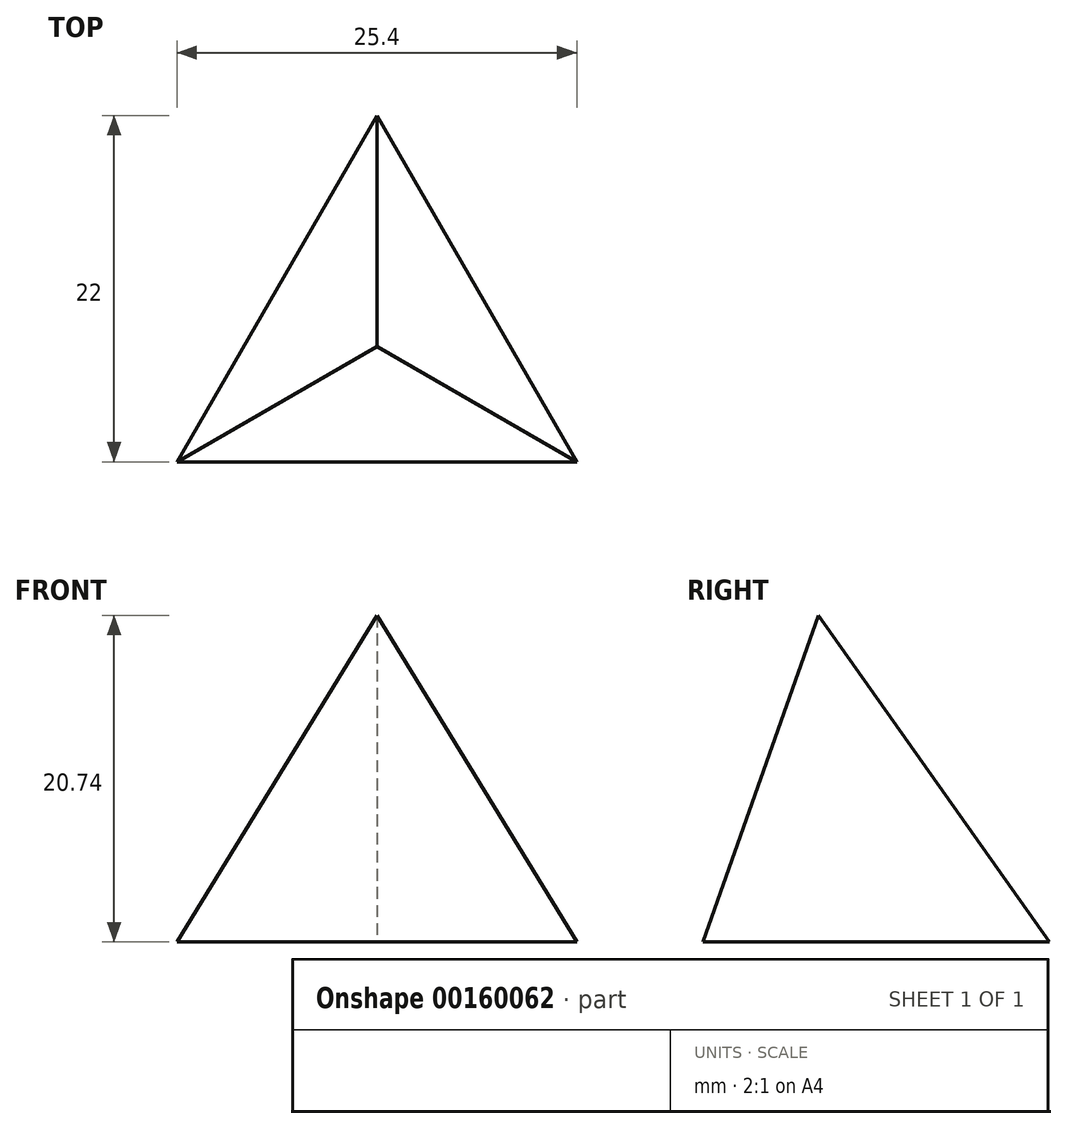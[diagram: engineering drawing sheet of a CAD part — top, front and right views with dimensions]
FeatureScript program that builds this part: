
annotation { "Feature Type Name" : "Feature", "Feature Type Description" : "" }
export const myFeature = defineFeature(function(context is Context, id is Id, definition is map)
    precondition{}
    {
        {
            var Q0;
            Q0=qCreatedBy(makeId("Top.planeOp"),FACE);
            var sketch = newSketch(context, id + "F0", { "sketchPlane" : qUnion([Q0])});
            skLineSegment(sketch, "E0", {"start": v(-12.7, 0) * mm, "end": v(0, 22) * mm});
            skLineSegment(sketch, "E1", {"start": v(0, 22) * mm, "end": v(12.7, 0) * mm});
            skLineSegment(sketch, "E2", {"start": v(12.7, 0) * mm, "end": v(-12.7, 0) * mm});
            skSolve(sketch);
        }
        {
            var Q0;
            Q0 = qSketchRegion(id + "F0", true);
            extrude(context, id + "F1", {"entities" : qUnion([Q0]), "depth" : 25.4 * mm, "hasDraft" : true, "draftAngle" : 90 * degree - atan(2 * (2 ^ 0.5)), "draftPullDirection" : true});
        }
    });
